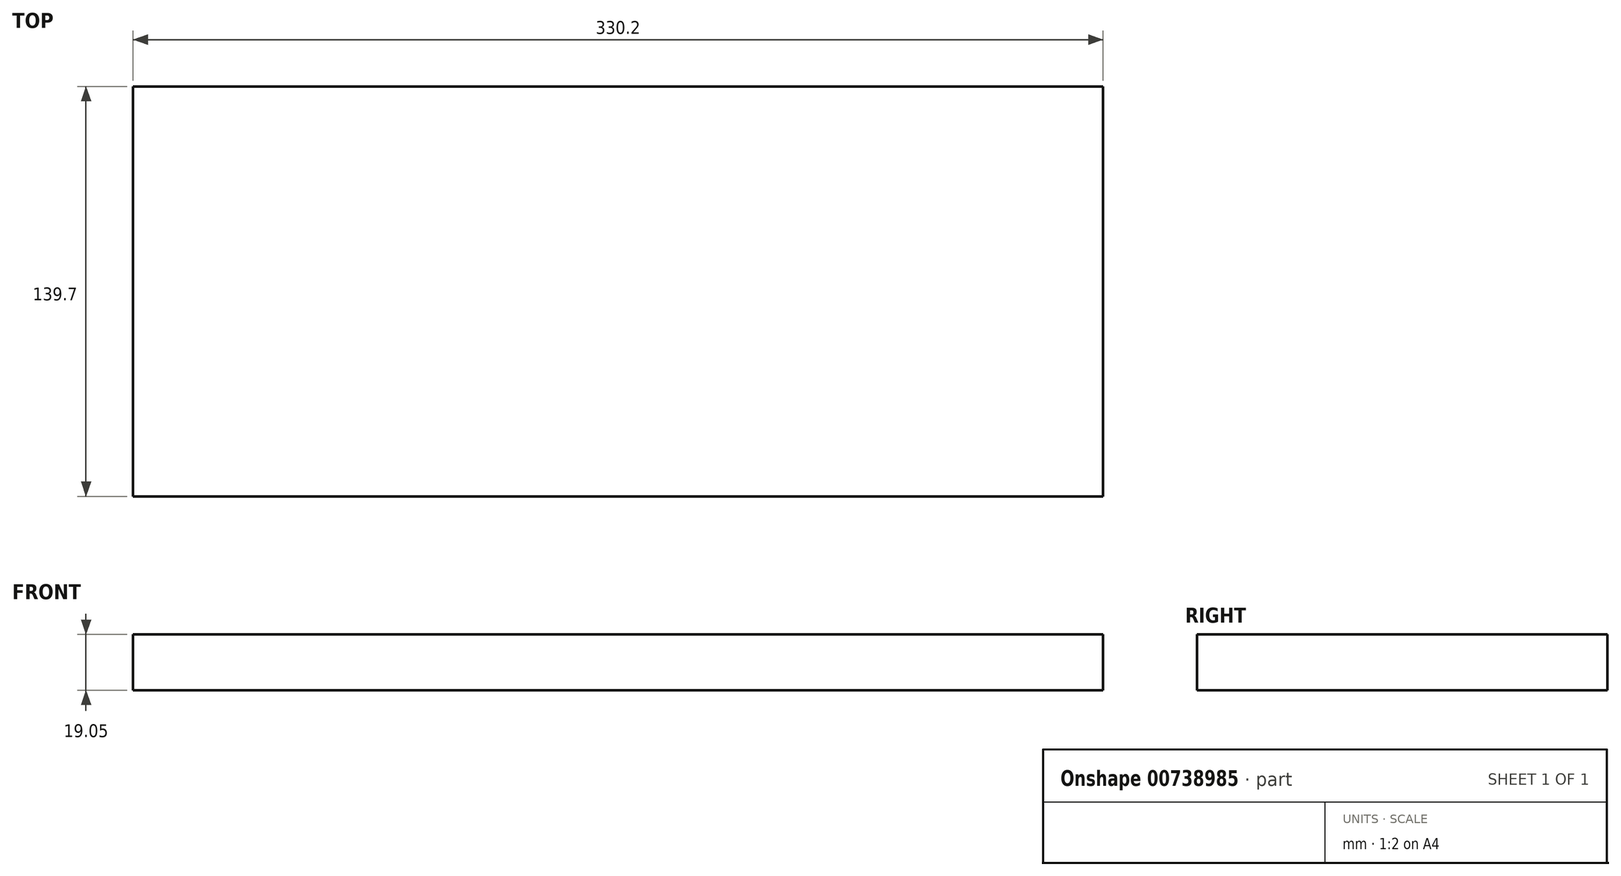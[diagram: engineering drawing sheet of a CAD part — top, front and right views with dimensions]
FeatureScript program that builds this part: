
annotation { "Feature Type Name" : "Feature", "Feature Type Description" : "" }
export const myFeature = defineFeature(function(context is Context, id is Id, definition is map)
    precondition{}
    {
        {
            var Q0;
            Q0=qCreatedBy(makeId("Top.planeOp"),FACE);
            var sketch = newSketch(context, id + "F0", { "sketchPlane" : qUnion([Q0])});
            skLineSegment(sketch, "E0.bottom", {"start": v(-60.77, 0) * mm, "end": v(269.43, 0) * mm});
            skLineSegment(sketch, "E0.top", {"start": v(-60.77, 139.7) * mm, "end": v(269.43, 139.7) * mm});
            skLineSegment(sketch, "E0.left", {"start": v(-60.77, 0) * mm, "end": v(-60.77, 139.7) * mm});
            skLineSegment(sketch, "E0.right", {"start": v(269.43, 0) * mm, "end": v(269.43, 139.7) * mm});
            skSolve(sketch);
        }
        {
            var Q0;
            Q0=qSketchRegion(id+"F0",true);
            extrude(context, id + "F1", {"entities" : qUnion([Q0]), "depth" : 19.05 * mm, "offsetDistance" : 25.4 * mm});
        }
    });
